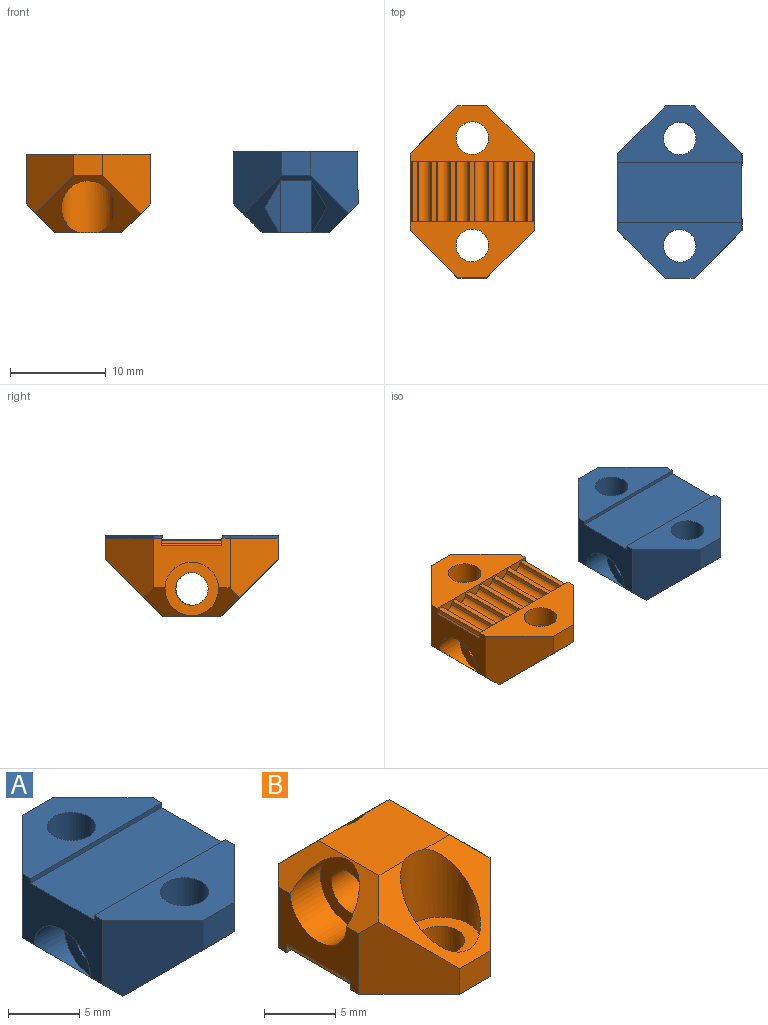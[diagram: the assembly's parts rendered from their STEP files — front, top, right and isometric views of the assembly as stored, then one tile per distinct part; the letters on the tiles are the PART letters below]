
ASSEMBLY  parts=2 mates=1
PART A: 44 faces, bbox 13x18x8.5 mm
  f0: plane 8x5.5mm, normal (1,0,0), area 28.5mm2, adj f8,f9,f10,f11,f12,f29,f30,f31
  f1: cylinder r=1.7mm len=7mm, axis (-1,0,0), area 74.8mm2, adj f27,f35
  f2: plane 7x6mm, normal (0,0,-1), area 40.7mm2, adj f13,f14,f15,f23,f24,f25,f40,f41
  f3: cylinder r=1.7mm len=3.4mm, axis (0,0,1), area 26.7mm2, adj f12,f26
  f4: cylinder r=1.7mm len=3.4mm, axis (0,0,1), area 26.7mm2, adj f11,f19
  f5: plane 8x5.5mm, normal (-1,0,0), area 29.7mm2, adj f8,f9,f10,f11,f12,f28,f37,f38
  f6: plane 3x2.5mm, normal (0,-1,0), area 7.5mm2, adj f12,f36,f37,f40
  f7: plane 3x2.5mm, normal (0,1,0), area 7.5mm2, adj f11,f38,f39,f41
  f8: plane 13x0.4mm, normal (0,1,0), area 5.3mm2, adj f0,f5,f10,f12
  f9: plane 13x0.4mm, normal (0,-1,0), area 5.3mm2, adj f0,f5,f10,f11
  f10: plane 13x6.3mm, normal (0,0,1), area 81.9mm2, adj f0,f5,f8,f9
  f11: plane 13x5.85mm, normal (0,0,1), area 42mm2, adj f0,f4,f5,f7,f9,f38,f39
  f12: plane 13x5.85mm, normal (0,0,1), area 42mm2, adj f0,f3,f5,f6,f8,f36,f37
  f13: plane 6x2.8mm, normal (-0.87,0.5,0), area 15.5mm2, adj f2,f14,f18,f19,f41
  f14: plane 6x3.23mm, normal (0,1,0), area 19.4mm2, adj f2,f13,f15,f19
  f15: plane 6x2.8mm, normal (0.87,0.5,0), area 15.5mm2, adj f2,f14,f16,f19,f41
  f16: plane 3.4x2.8mm, normal (0.87,-0.5,0), area 6.5mm2, adj f15,f17,f19,f41
  f17: plane 3.23x0.6mm, normal (0,-1,0), area 1.9mm2, adj f16,f18,f19,f41
  f18: plane 3.4x2.8mm, normal (-0.87,-0.5,0), area 6.5mm2, adj f13,f17,f19,f41
  f19: plane 6.47x5.6mm, normal (0,0,-1), area 18.1mm2, adj f4,f13,f14,f15,f16,f17,f18
  f20: plane 3.4x2.8mm, normal (-0.87,0.5,0), area 6.5mm2, adj f21,f25,f26,f40
  f21: plane 3.23x0.6mm, normal (0,1,0), area 1.9mm2, adj f20,f22,f26,f40
  f22: plane 3.4x2.8mm, normal (0.87,0.5,0), area 6.5mm2, adj f21,f23,f26,f40
  f23: plane 6x2.8mm, normal (0.87,-0.5,0), area 15.5mm2, adj f2,f22,f24,f26,f40
  f24: plane 6x3.23mm, normal (0,-1,0), area 19.4mm2, adj f2,f23,f25,f26
  f25: plane 6x2.8mm, normal (-0.87,-0.5,0), area 15.5mm2, adj f2,f20,f24,f26,f40
  f26: plane 6.47x5.6mm, normal (0,0,-1), area 18.1mm2, adj f3,f20,f21,f22,f23,f24,f25
  f27: plane 5.6x5.6mm, normal (-1,0,0), area 15.6mm2, adj f1,f28
  f28: cylinder r=2.8mm len=5.6mm, axis (-1,0,0), area 36.2mm2, adj f5,f27,f42
  f29: plane 3x2.8mm, normal (0,-0.87,-0.5), area 9.7mm2, adj f0,f30,f34,f35,f43
  f30: plane 3.23x3mm, normal (0,0,-1), area 9.7mm2, adj f0,f29,f31,f35
  f31: plane 3x2.8mm, normal (0,0.87,-0.5), area 9.7mm2, adj f0,f30,f32,f35,f43
  f32: plane 2.9x2.8mm, normal (0,0.87,0.5), area 4.8mm2, adj f31,f33,f35,f43
  f33: plane 3.23x0.1mm, normal (0,0,1), area 0.3mm2, adj f32,f34,f35,f43
  f34: plane 2.9x2.8mm, normal (0,-0.87,0.5), area 4.8mm2, adj f29,f33,f35,f43
  f35: plane 6.47x5.6mm, normal (1,0,0), area 18.1mm2, adj f1,f29,f30,f31,f32,f33,f34
  f36: plane 6.5x5mm, normal (0.71,-0.71,0), area 33.9mm2, adj f0,f6,f12,f40,f43
  f37: plane 6.5x5mm, normal (-0.71,-0.71,0), area 33.9mm2, adj f5,f6,f12,f40,f42
  f38: plane 6.5x5mm, normal (-0.71,0.71,0), area 33.9mm2, adj f5,f7,f11,f41,f42
  f39: plane 6.5x5mm, normal (0.71,0.71,0), area 33.9mm2, adj f0,f7,f11,f41,f43
  f40: plane 11x6mm, normal (0,-0.71,-0.71), area 27.6mm2, adj f2,f6,f20,f21,f22,f23,f25,f36
  f41: plane 11x6mm, normal (0,0.71,-0.71), area 27.6mm2, adj f2,f7,f13,f15,f16,f17,f18,f38
  f42: plane 10x3mm, normal (-0.71,0,-0.71), area 17.1mm2, adj f2,f5,f28,f37,f38,f40,f41
  f43: plane 10x3mm, normal (0.71,0,-0.71), area 15.2mm2, adj f0,f2,f29,f31,f32,f33,f34,f36
PART B: 62 faces, bbox 13.5x18.5x8.7 mm
  f0: plane 8x5.2mm, normal (1,0,0), area 23.8mm2, adj f31,f32,f33,f37,f38,f48,f49,f50
  f1: cylinder r=1.7mm len=7mm, axis (-1,0,0), area 74.8mm2, adj f45,f53
  f2: plane 7x6mm, normal (0,0,1), area 41.4mm2, adj f41,f44,f58,f59,f60,f61
  f3: cylinder r=0.7mm len=6.3mm, axis (0,1,0), area 1.5mm2, adj f4,f32,f33,f36
  f4: cylinder r=1.15mm len=6.3mm, axis (0,1,0), area 2.3mm2, adj f3,f5,f32,f33
  f5: plane 6.3x0.52mm, normal (0,0,-1), area 3.3mm2, adj f4,f6,f32,f33
  f6: cylinder r=1.15mm len=6.3mm, axis (0,1,0), area 2.3mm2, adj f5,f7,f32,f33
  f7: cylinder r=0.7mm len=6.3mm, axis (0,1,0), area 9.9mm2, adj f6,f8,f32,f33
  f8: cylinder r=1.15mm len=6.3mm, axis (0,1,0), area 2.3mm2, adj f7,f9,f32,f33
  f9: plane 6.3x0.52mm, normal (0,0,-1), area 3.3mm2, adj f8,f10,f32,f33
  f10: cylinder r=1.15mm len=6.3mm, axis (0,1,0), area 2.3mm2, adj f9,f11,f32,f33
  f11: cylinder r=0.7mm len=6.3mm, axis (0,1,0), area 9.9mm2, adj f10,f12,f32,f33
  f12: cylinder r=1.15mm len=6.3mm, axis (0,1,0), area 2.3mm2, adj f11,f13,f32,f33
  f13: plane 6.3x0.52mm, normal (0,0,-1), area 3.3mm2, adj f12,f14,f32,f33
  f14: cylinder r=1.15mm len=6.3mm, axis (0,1,0), area 2.3mm2, adj f13,f15,f32,f33
  f15: cylinder r=0.7mm len=6.3mm, axis (0,1,0), area 9.9mm2, adj f14,f16,f32,f33
  f16: cylinder r=1.15mm len=6.3mm, axis (0,1,0), area 2.3mm2, adj f15,f17,f32,f33
  f17: plane 6.3x0.52mm, normal (0,0,-1), area 3.3mm2, adj f16,f18,f32,f33
  f18: cylinder r=1.15mm len=6.3mm, axis (0,1,0), area 2.3mm2, adj f17,f19,f32,f33
  f19: cylinder r=0.7mm len=6.3mm, axis (0,1,0), area 9.9mm2, adj f18,f20,f32,f33
  f20: cylinder r=1.15mm len=6.3mm, axis (0,1,0), area 2.3mm2, adj f19,f21,f32,f33
  f21: plane 6.3x0.52mm, normal (0,0,-1), area 3.3mm2, adj f20,f22,f32,f33
  f22: cylinder r=1.15mm len=6.3mm, axis (0,1,0), area 2.3mm2, adj f21,f23,f32,f33
  f23: cylinder r=0.7mm len=6.3mm, axis (0,1,0), area 9.9mm2, adj f22,f24,f32,f33
  f24: cylinder r=1.15mm len=6.3mm, axis (0,1,0), area 2.3mm2, adj f23,f25,f32,f33
  f25: plane 6.3x0.52mm, normal (0,0,-1), area 3.3mm2, adj f24,f26,f32,f33
  f26: cylinder r=1.15mm len=6.3mm, axis (0,1,0), area 2.3mm2, adj f25,f27,f32,f33
  f27: cylinder r=0.7mm len=6.3mm, axis (0,1,0), area 9.9mm2, adj f26,f28,f32,f33
  f28: cylinder r=1.15mm len=6.3mm, axis (0,1,0), area 2.3mm2, adj f27,f29,f32,f33
  f29: plane 6.3x0.52mm, normal (0,0,-1), area 3.3mm2, adj f28,f30,f32,f33
  f30: cylinder r=1.15mm len=6.3mm, axis (0,1,0), area 2.3mm2, adj f29,f31,f32,f33
  f31: cylinder r=0.7mm len=6.3mm, axis (0,1,0), area 1.5mm2, adj f0,f30,f32,f33
  f32: plane 13x0.98mm, normal (0,1,0), area 8.2mm2, adj f0,f3,f4,f5,f6,f7,f8,f9
  f33: plane 13x0.98mm, normal (0,-1,0), area 8.2mm2, adj f0,f3,f4,f5,f6,f7,f8,f9
  f34: plane 3x2.2mm, normal (0,1,0), area 6.6mm2, adj f38,f54,f57,f58
  f35: plane 3x2.2mm, normal (0,-1,0), area 6.6mm2, adj f37,f55,f56,f59
  f36: plane 8x5.2mm, normal (-1,0,0), area 25mm2, adj f3,f32,f33,f37,f38,f46,f54,f55
  f37: plane 13x5.85mm, normal (0,0,-1), area 42mm2, adj f0,f32,f35,f36,f39,f55,f56
  f38: plane 13x5.85mm, normal (0,0,-1), area 42mm2, adj f0,f33,f34,f36,f42,f54,f57
  f39: cylinder r=1.7mm len=3.4mm, axis (0,0,1), area 23.5mm2, adj f37,f40
  f40: plane 5.6x5.6mm, normal (0,0,1), area 15.6mm2, adj f39,f41
  f41: cylinder r=2.8mm len=6mm, axis (0,0,1), area 58.9mm2, adj f2,f40,f59
  f42: cylinder r=1.7mm len=3.4mm, axis (0,0,1), area 23.5mm2, adj f38,f43
  f43: plane 5.6x5.6mm, normal (0,0,1), area 15.6mm2, adj f42,f44
  f44: cylinder r=2.8mm len=6mm, axis (0,0,1), area 58.9mm2, adj f2,f43,f58
  f45: plane 5.6x5.6mm, normal (-1,0,0), area 15.6mm2, adj f1,f46
  f46: cylinder r=2.8mm len=5.6mm, axis (-1,0,0), area 36.2mm2, adj f36,f45,f61
  f47: plane 2.9x2.8mm, normal (0,0.87,-0.5), area 4.8mm2, adj f48,f52,f53,f60
  f48: plane 3x2.8mm, normal (0,0.87,0.5), area 9.7mm2, adj f0,f47,f49,f53,f60
  f49: plane 3.23x3mm, normal (0,0,1), area 9.7mm2, adj f0,f48,f50,f53
  f50: plane 3x2.8mm, normal (0,-0.87,0.5), area 9.7mm2, adj f0,f49,f51,f53,f60
  f51: plane 2.9x2.8mm, normal (0,-0.87,-0.5), area 4.8mm2, adj f50,f52,f53,f60
  f52: plane 3.23x0.1mm, normal (0,0,-1), area 0.3mm2, adj f47,f51,f53,f60
  f53: plane 6.47x5.6mm, normal (1,0,0), area 18.1mm2, adj f1,f47,f48,f49,f50,f51,f52
  f54: plane 6.2x5mm, normal (-0.71,0.71,0), area 31.8mm2, adj f34,f36,f38,f58,f61
  f55: plane 6.2x5mm, normal (-0.71,-0.71,0), area 31.8mm2, adj f35,f36,f37,f59,f61
  f56: plane 6.2x5mm, normal (0.71,-0.71,0), area 31.8mm2, adj f0,f35,f37,f59,f60
  f57: plane 6.2x5mm, normal (0.71,0.71,0), area 31.8mm2, adj f0,f34,f38,f58,f60
  f58: plane 11.55x6.55mm, normal (0,0.71,0.71), area 30.6mm2, adj f2,f34,f44,f54,f57,f60,f61
  f59: plane 11.55x6.55mm, normal (0,-0.71,0.71), area 30.6mm2, adj f2,f35,f41,f55,f56,f60,f61
  f60: plane 10x3mm, normal (0.71,0,0.71), area 15.2mm2, adj f0,f2,f47,f48,f50,f51,f52,f56
  f61: plane 10x3mm, normal (-0.71,0,0.71), area 17.1mm2, adj f2,f36,f46,f54,f55,f58,f59
PLACE A t=(11.21,-0.38,-2.42)mm
PLACE B rot(axis=(1,0,0),180deg) t=(-10.44,-0.33,-2.42)mm
MATE planar A.f2 <-> B.f2  axis (0,0,-1) through (7.71,-0.38,-10.92)mm
